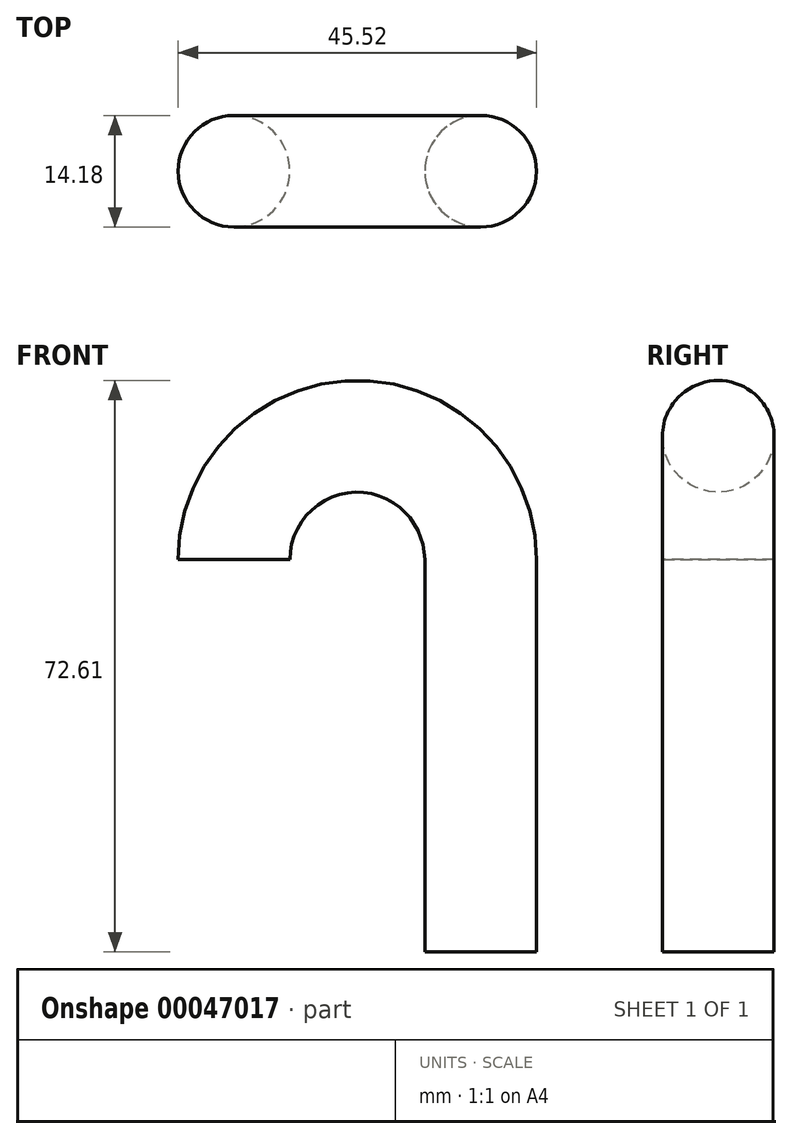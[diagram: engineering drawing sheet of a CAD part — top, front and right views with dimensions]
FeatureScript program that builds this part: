
annotation { "Feature Type Name" : "Feature", "Feature Type Description" : "" }
export const myFeature = defineFeature(function(context is Context, id is Id, definition is map)
    precondition{}
    {
        {
            var Q0;
            Q0=qCreatedBy(makeId("Front.planeOp"),FACE);
            var sketch = newSketch(context, id + "F0", { "sketchPlane" : qUnion([Q0])});
            skLineSegment(sketch, "E0", {"start": v(0, 0) * mm, "end": v(0, 49.85) * mm});
            skArc(sketch, "E1", {"start": v(0, 49.85) * mm, "mid": v(-15.67, 65.52) * mm, "end": v(-31.34, 49.85) * mm});
            skSolve(sketch);
        }
        {
            var Q0;
            Q0=qCreatedBy(makeId("Top.planeOp"),FACE);
            var sketch = newSketch(context, id + "F1", { "sketchPlane" : qUnion([Q0])});
            skCircle(sketch, "E2", {"center": v(0, 0) * mm, "radius": 7.1 * mm});
            skSolve(sketch);
        }
        {
            var Q0;
            Q0=makeQuery(id+"F1.imprint","IMPRINT",FACE,{"disambiguationData":[TD([[makeQuery(id+"F1.imprint","IMPRINT",EDGE,{"derivedFrom":sQuery(id+"F1.wireOp",EDGE,"E2")}),1.0]])]});
            var Q1;
            Q1=sQuery(id+"F0.wireOp",EDGE,"E0");
            var Q2;
            Q2=sQuery(id+"F0.wireOp",EDGE,"E1");
            sweep(context, id + "F2", {"profiles" : qUnion([Q0]), "path" : qUnion([Q1, Q2])});
        }
    });
